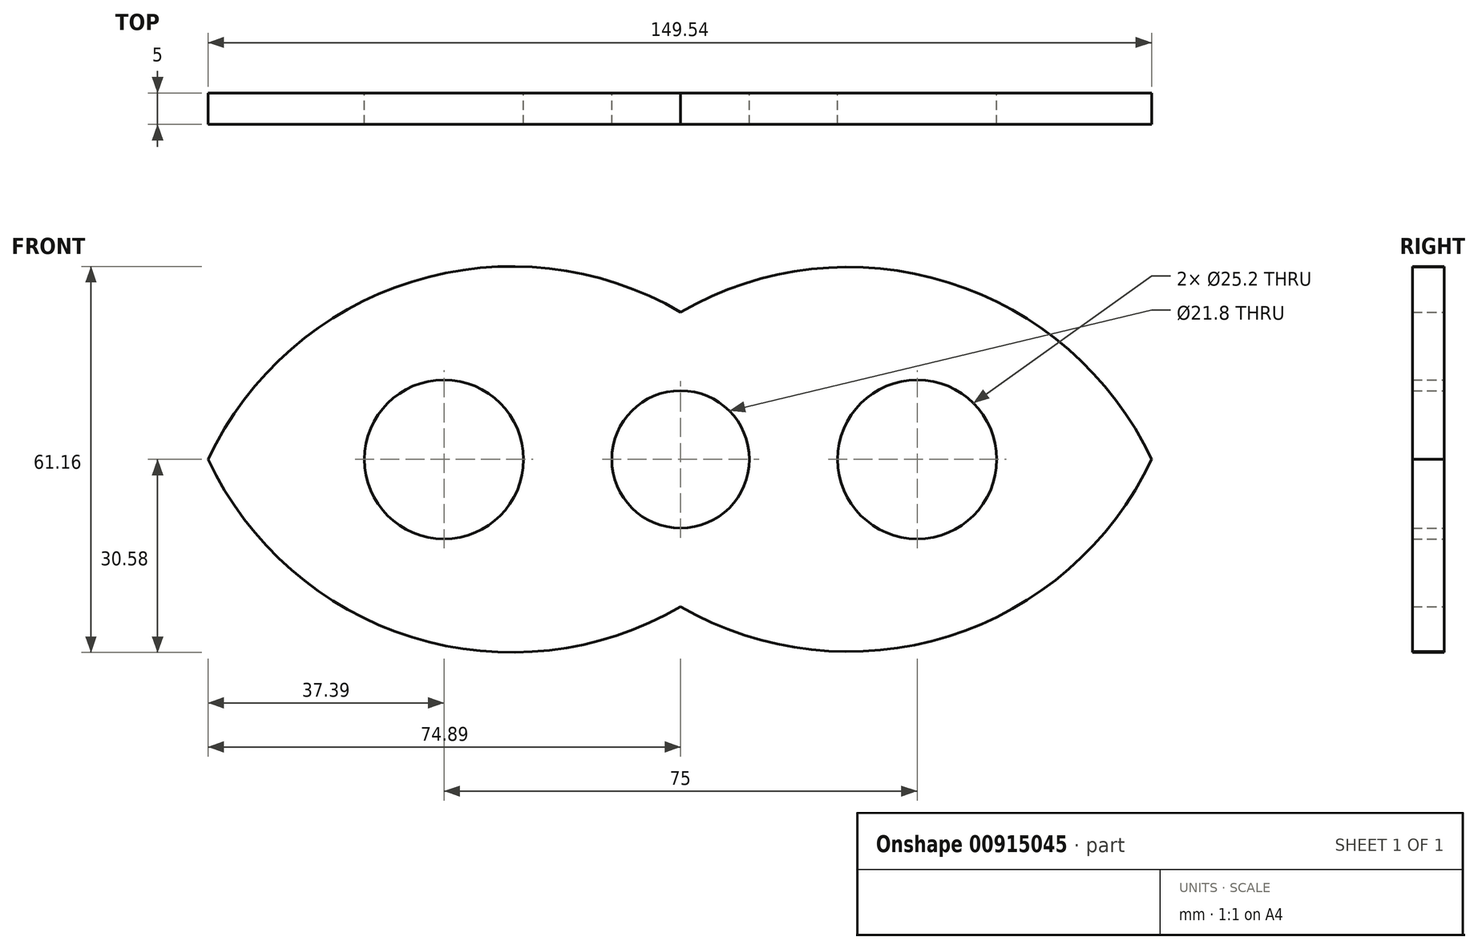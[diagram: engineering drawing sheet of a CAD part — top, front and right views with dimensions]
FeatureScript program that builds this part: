
annotation { "Feature Type Name" : "Feature", "Feature Type Description" : "" }
export const myFeature = defineFeature(function(context is Context, id is Id, definition is map)
    precondition{}
    {
        {
            var Q0;
            Q0=qCreatedBy(makeId("Front.planeOp"),FACE);
            var sketch = newSketch(context, id + "F0", { "sketchPlane" : qUnion([Q0])});
            skCircle(sketch, "E0", {"center": v(0, 0) * mm, "radius": 10.9 * mm});
            skCircle(sketch, "E1", {"center": v(37.5, 0) * mm, "radius": 12.6 * mm});
            skCircle(sketch, "E2", {"center": v(-37.5, 0) * mm, "radius": 12.6 * mm});
            skArc(sketch, "E3", {"start": v(0, 23.36) * mm, "mid": v(-42.59, 28.17) * mm, "end": v(-74.89, 0) * mm});
            skArc(sketch, "E4", {"start": v(74.65, 0) * mm, "mid": v(42.45, 28.05) * mm, "end": v(0, 23.36) * mm});
            skArc(sketch, "E5", {"start": v(0, -23.36) * mm, "mid": v(42.45, -28.05) * mm, "end": v(74.65, 0) * mm});
            skArc(sketch, "E6", {"start": v(-74.89, 0) * mm, "mid": v(-42.59, -28.17) * mm, "end": v(0, -23.36) * mm});
            skSolve(sketch);
        }
        {
            var Q0;
            Q0=makeQuery(id+"F0.imprint","IMPRINT",FACE,{"disambiguationData":[TD([[makeQuery(id+"F0.imprint","IMPRINT",EDGE,{"derivedFrom":sQuery(id+"F0.wireOp",EDGE,"FhWvOTSn-KdVi-aaoh-95DT-xfM0dzBvxnID")}),-1.0]])]});
            var Q1;
            Q1=makeQuery(id+"F0.imprint","IMPRINT",FACE,{"disambiguationData":[TD([[makeQuery(id+"F0.imprint","IMPRINT",EDGE,{"derivedFrom":sQuery(id+"F0.wireOp",EDGE,"E0")}),-1.0]])]});
            extrude(context, id + "F1", {"entities" : qUnion([Q0, Q1]), "depth" : 5 * mm, "offsetDistance" : 25 * mm});
        }
    });
